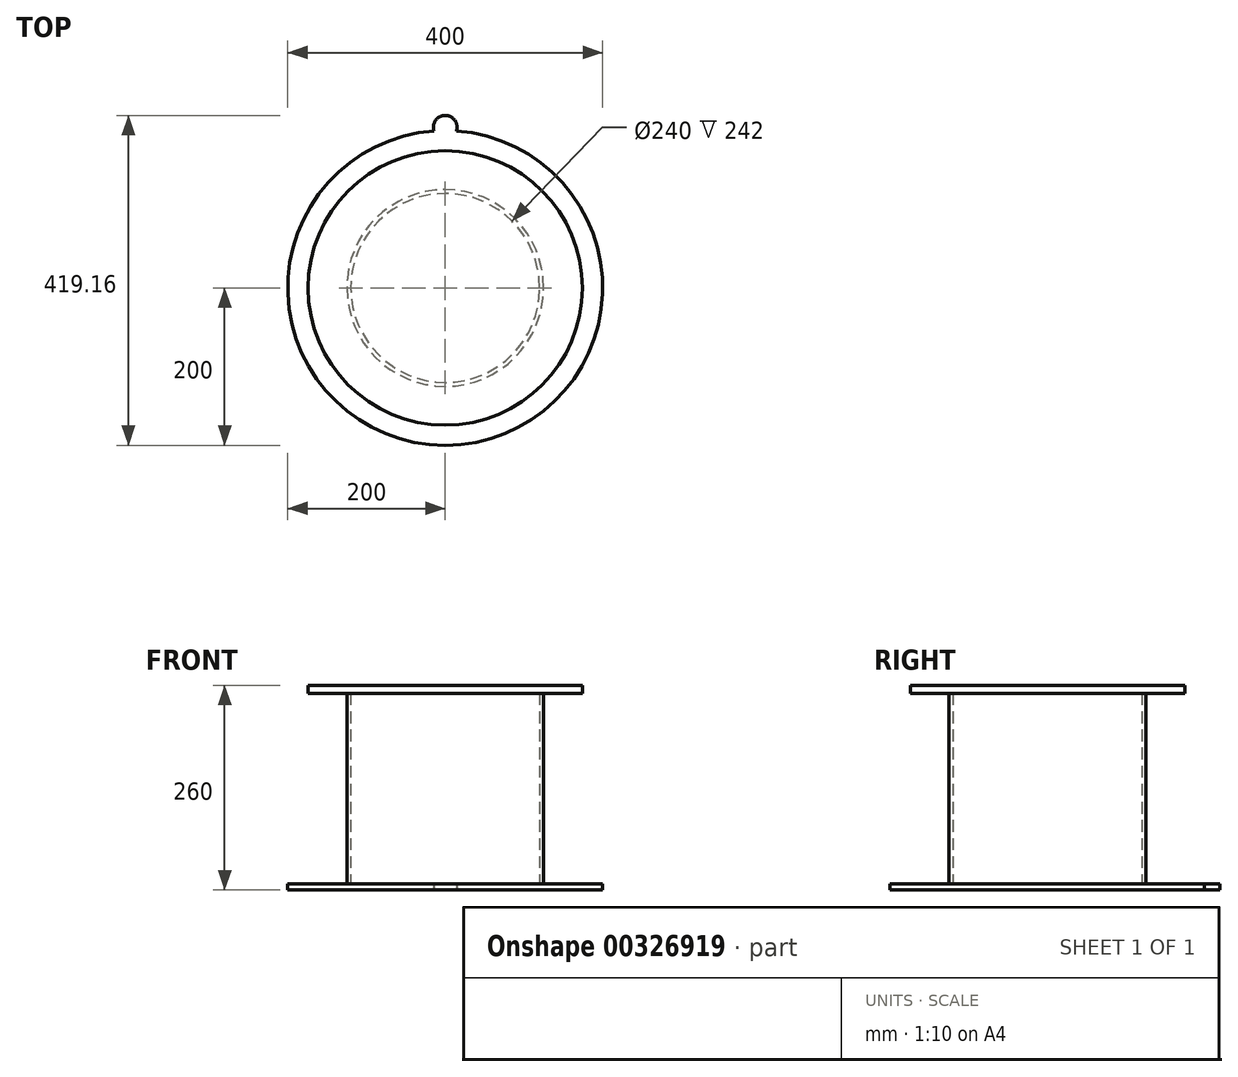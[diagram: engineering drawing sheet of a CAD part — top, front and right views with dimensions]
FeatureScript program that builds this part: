
annotation { "Feature Type Name" : "Feature", "Feature Type Description" : "" }
export const myFeature = defineFeature(function(context is Context, id is Id, definition is map)
    precondition{}
    {
        {
            var Q0;
            Q0=qCreatedBy(makeId("Top.planeOp"),FACE);
            var sketch = newSketch(context, id + "F0", { "sketchPlane" : qUnion([Q0])});
            skCircle(sketch, "E0", {"center": v(0, 0) * mm, "radius": 125 * mm});
            skCircle(sketch, "E1", {"center": v(0, 0) * mm, "radius": 120 * mm});
            skSolve(sketch);
        }
        {
            var Q0;
            Q0=makeQuery(id+"F0.imprint","IMPRINT",FACE,{"disambiguationData":[TD([[makeQuery(id+"F0.imprint","IMPRINT",EDGE,{"derivedFrom":sQuery(id+"F0.wireOp",EDGE,"E0")}),1.0]])]});
            extrude(context, id + "F1", {"entities" : qUnion([Q0]), "depth" : 250 * mm});
        }
        {
            var Q0;
            Q0=qCreatedBy(makeId("Top.planeOp"),FACE);
            var sketch = newSketch(context, id + "F2", { "sketchPlane" : qUnion([Q0])});
            skCircle(sketch, "E2", {"center": v(0, 204.16) * mm, "radius": 15 * mm});
            skCircle(sketch, "E3", {"center": v(0, 0) * mm, "radius": 200 * mm});
            skSolve(sketch);
        }
        {
            var Q0;
            Q0 = qSketchRegion(id + "F2", true);
            extrude(context, id + "F3", {"entities" : qUnion([Q0]), "operationType" : NewBodyOperationType.ADD, "depth" : 8 * mm});
        }
        {
            var Q0;
            Q0=makeQuery(id+"F1.opExtrude","CAP_FACE",FACE,{"disambiguationData":[OSD([sQuery(id+"F0.wireOp",EDGE,"E0"),sQuery(id+"F0.wireOp",EDGE,"E1")])],"isStart":false});
            var sketch = newSketch(context, id + "F4", { "sketchPlane" : qUnion([Q0])});
            skCircle(sketch, "E4", {"center": v(0, 0) * mm, "radius": 174.28 * mm});
            skSolve(sketch);
        }
        {
            var Q0;
            Q0 = qSketchRegion(id + "F4", true);
            extrude(context, id + "F5", {"entities" : qUnion([Q0]), "operationType" : NewBodyOperationType.ADD, "depth" : 10 * mm});
        }
    });
